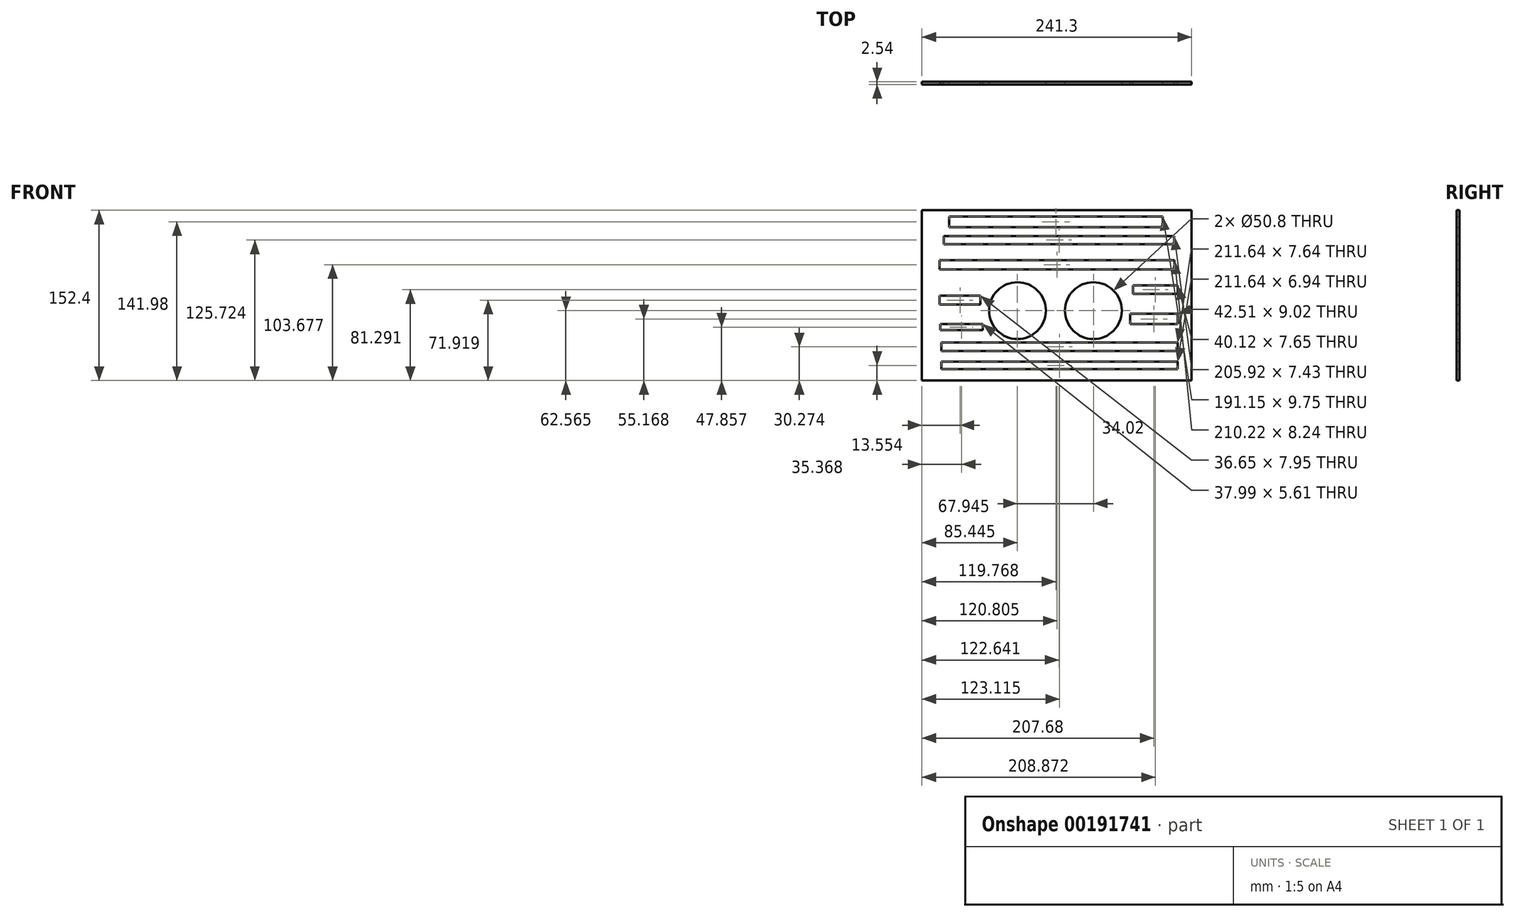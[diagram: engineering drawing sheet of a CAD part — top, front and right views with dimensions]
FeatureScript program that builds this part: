
annotation { "Feature Type Name" : "Feature", "Feature Type Description" : "" }
export const myFeature = defineFeature(function(context is Context, id is Id, definition is map)
    precondition{}
    {
        {
            var Q0;
            Q0=qCreatedBy(makeId("Front.planeOp"),FACE);
            var sketch = newSketch(context, id + "F0", { "sketchPlane" : qUnion([Q0])});
            skLineSegment(sketch, "E0.bottom", {"start": v(-153.4, 101.74) * mm, "end": v(87.9, 101.74) * mm});
            skLineSegment(sketch, "E0.top", {"start": v(-153.4, -50.66) * mm, "end": v(87.9, -50.66) * mm});
            skLineSegment(sketch, "E0.left", {"start": v(-153.4, 101.74) * mm, "end": v(-153.4, -50.66) * mm});
            skLineSegment(sketch, "E0.right", {"start": v(87.9, 101.74) * mm, "end": v(87.9, -50.66) * mm});
            skCircle(sketch, "E1", {"center": v(-67.95, 11.9) * mm, "radius": 25.4 * mm});
            skCircle(sketch, "E2", {"center": v(0, 11.9) * mm, "radius": 25.4 * mm});
            skLineSegment(sketch, "E3.bottom", {"start": v(75.54, -16.56) * mm, "end": v(-136.1, -16.56) * mm});
            skLineSegment(sketch, "E3.top", {"start": v(75.54, -24.2) * mm, "end": v(-136.1, -24.2) * mm});
            skLineSegment(sketch, "E3.left", {"start": v(75.54, -16.56) * mm, "end": v(75.54, -24.2) * mm});
            skLineSegment(sketch, "E3.right", {"start": v(-136.1, -16.56) * mm, "end": v(-136.1, -24.2) * mm});
            skLineSegment(sketch, "E4.bottom", {"start": v(75.54, -33.64) * mm, "end": v(-136.1, -33.64) * mm});
            skLineSegment(sketch, "E4.top", {"start": v(75.54, -40.57) * mm, "end": v(-136.1, -40.57) * mm});
            skLineSegment(sketch, "E4.left", {"start": v(75.54, -33.64) * mm, "end": v(75.54, -40.57) * mm});
            skLineSegment(sketch, "E4.right", {"start": v(-136.1, -33.64) * mm, "end": v(-136.1, -40.57) * mm});
            skLineSegment(sketch, "E5.bottom", {"start": v(75.54, 9.02) * mm, "end": v(33.04, 9.02) * mm});
            skLineSegment(sketch, "E5.top", {"start": v(75.54, 0) * mm, "end": v(33.04, 0) * mm});
            skLineSegment(sketch, "E5.left", {"start": v(75.54, 9.02) * mm, "end": v(75.54, 0) * mm});
            skLineSegment(sketch, "E5.right", {"start": v(33.04, 9.02) * mm, "end": v(33.04, 0) * mm});
            skLineSegment(sketch, "E6.bottom", {"start": v(75.54, 34.46) * mm, "end": v(35.42, 34.46) * mm});
            skLineSegment(sketch, "E6.top", {"start": v(75.54, 26.8) * mm, "end": v(35.42, 26.8) * mm});
            skLineSegment(sketch, "E6.left", {"start": v(75.54, 34.46) * mm, "end": v(75.54, 26.8) * mm});
            skLineSegment(sketch, "E6.right", {"start": v(35.42, 34.46) * mm, "end": v(35.42, 26.8) * mm});
            skLineSegment(sketch, "E7.right", {"start": v(-86.01, 29.76) * mm, "end": v(-86.01, 29.45) * mm});
            skLineSegment(sketch, "E8.bottom", {"start": v(-99.03, -5.6) * mm, "end": v(-137.02, -5.6) * mm});
            skLineSegment(sketch, "E8.top", {"start": v(-99.03, 0) * mm, "end": v(-137.02, 0) * mm});
            skLineSegment(sketch, "E8.left", {"start": v(-99.03, -5.6) * mm, "end": v(-99.03, 0) * mm});
            skLineSegment(sketch, "E8.right", {"start": v(-137.02, -5.6) * mm, "end": v(-137.02, 0) * mm});
            skLineSegment(sketch, "E9.bottom", {"start": v(-101.04, 25.23) * mm, "end": v(-137.7, 25.23) * mm});
            skLineSegment(sketch, "E9.top", {"start": v(-101.04, 17.28) * mm, "end": v(-137.7, 17.28) * mm});
            skLineSegment(sketch, "E9.left", {"start": v(-101.04, 17.28) * mm, "end": v(-101.04, 25.23) * mm});
            skLineSegment(sketch, "E9.right", {"start": v(-137.7, 17.28) * mm, "end": v(-137.7, 25.23) * mm});
            skLineSegment(sketch, "E10.bottom", {"start": v(72.53, 48.9) * mm, "end": v(-137.7, 48.9) * mm});
            skLineSegment(sketch, "E10.top", {"start": v(72.53, 57.14) * mm, "end": v(-137.7, 57.14) * mm});
            skLineSegment(sketch, "E10.left", {"start": v(72.53, 48.9) * mm, "end": v(72.53, 57.14) * mm});
            skLineSegment(sketch, "E10.right", {"start": v(-137.7, 48.9) * mm, "end": v(-137.7, 57.14) * mm});
            skLineSegment(sketch, "E11.bottom", {"start": v(-133.7, 71.35) * mm, "end": v(72.21, 71.35) * mm});
            skLineSegment(sketch, "E11.top", {"start": v(-133.7, 78.78) * mm, "end": v(72.21, 78.78) * mm});
            skLineSegment(sketch, "E11.left", {"start": v(-133.7, 71.35) * mm, "end": v(-133.7, 78.78) * mm});
            skLineSegment(sketch, "E11.right", {"start": v(72.21, 71.35) * mm, "end": v(72.21, 78.78) * mm});
            skLineSegment(sketch, "E12.bottom", {"start": v(-129.2, 96.2) * mm, "end": v(61.95, 96.2) * mm});
            skLineSegment(sketch, "E12.top", {"start": v(-129.2, 86.44) * mm, "end": v(61.95, 86.44) * mm});
            skLineSegment(sketch, "E12.left", {"start": v(-129.2, 86.44) * mm, "end": v(-129.2, 96.2) * mm});
            skLineSegment(sketch, "E12.right", {"start": v(61.95, 86.44) * mm, "end": v(61.95, 96.2) * mm});
            skSolve(sketch);
        }
        {
            var Q0;
            Q0 = qSketchRegion(id + "F0", true);
            var Q1;
            Q1=makeQuery(id+"F0.imprint","IMPRINT",FACE,{"disambiguationData":[TD([[makeQuery(id+"F0.imprint","IMPRINT",EDGE,{"derivedFrom":sQuery(id+"F0.wireOp",EDGE,"E0.bottom")}),-1.0]])]});
            extrude(context, id + "F1", {"entities" : qUnion([Q0, Q1]), "depth" : 2.54 * mm});
        }
        {
            var Q0;
            Q0 = qSketchRegion(id + "F0", true);
            extrude(context, id + "F2", {"entities" : qUnion([Q0]), "operationType" : NewBodyOperationType.ADD, "depth" : 2.54 * mm});
        }
    });
